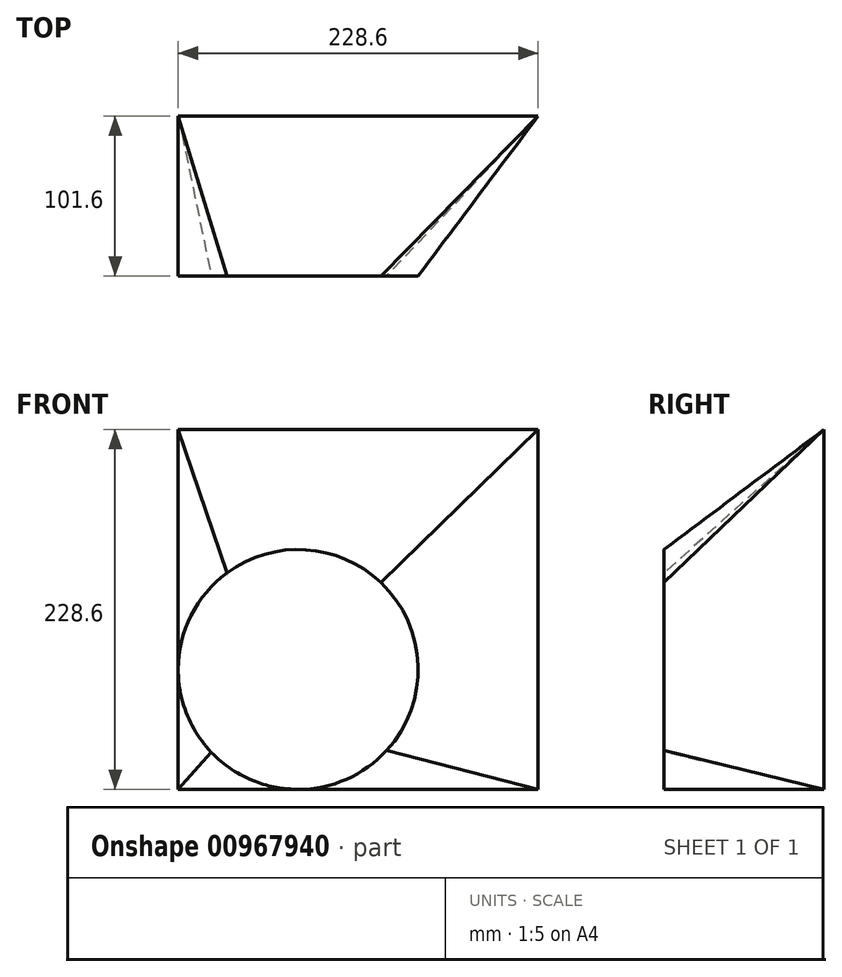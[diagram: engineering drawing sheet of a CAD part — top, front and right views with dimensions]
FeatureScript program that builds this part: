
annotation { "Feature Type Name" : "Feature", "Feature Type Description" : "" }
export const myFeature = defineFeature(function(context is Context, id is Id, definition is map)
    precondition{}
    {
        {
            var Q0;
            Q0=qCreatedBy(makeId("Front.planeOp"),FACE);
            var sketch = newSketch(context, id + "F0", { "sketchPlane" : qUnion([Q0])});
            skLineSegment(sketch, "E0.bottom", {"start": v(-114.3, 114.3) * mm, "end": v(114.3, 114.3) * mm});
            skLineSegment(sketch, "E0.top", {"start": v(-114.3, -114.3) * mm, "end": v(114.3, -114.3) * mm});
            skLineSegment(sketch, "E0.left", {"start": v(-114.3, 114.3) * mm, "end": v(-114.3, -114.3) * mm});
            skLineSegment(sketch, "E0.right", {"start": v(114.3, 114.3) * mm, "end": v(114.3, -114.3) * mm});
            skPoint(sketch, "E0.middle", {"position": v(0, 0) * mm});
            skSolve(sketch);
        }
        {
            var Q0;
            Q0=makeQuery(id+"F0.imprint","IMPRINT",FACE,{"disambiguationData":[TD([[makeQuery(id+"F0.imprint","IMPRINT",EDGE,{"derivedFrom":sQuery(id+"F0.wireOp",EDGE,"E0.bottom")}),-1.0]])]});
            cPlane(context, id + "F1", {"entities" : qUnion([Q0]), "cplaneType" : CPlaneType.OFFSET, "offset" : 101.6 * mm, "width" : 152.4 * mm, "height" : 152.4 * mm});
        }
        {
            var Q0;
            Q0=qCreatedBy(id+"F1.planeOp",FACE);
            var sketch = newSketch(context, id + "F2", { "sketchPlane" : qUnion([Q0])});
            skLineSegment(sketch, "E1", {"start": v(-114.3, 114.3) * mm, "end": v(-83.37, 23.2) * mm, "construction": true});
            skLineSegment(sketch, "E2", {"start": v(114.3, 114.3) * mm, "end": v(14.45, 17.08) * mm, "construction": true});
            skLineSegment(sketch, "E3", {"start": v(114.3, -114.3) * mm, "end": v(18.05, -89.62) * mm, "construction": true});
            skLineSegment(sketch, "E4", {"start": v(-114.3, -114.3) * mm, "end": v(-93.27, -90.66) * mm, "construction": true});
            skArc(sketch, "E5", {"start": v(-83.37, 23.2) * mm, "mid": v(-114.01, -31.5) * mm, "end": v(-93.27, -90.66) * mm});
            skArc(sketch, "E6", {"start": v(14.45, 17.08) * mm, "mid": v(-33.35, 37.95) * mm, "end": v(-83.37, 23.2) * mm});
            skLineSegment(sketch, "E7", {"start": v(18.05, -89.62) * mm, "end": v(18.05, -89.62) * mm});
            skLineSegment(sketch, "E8", {"start": v(14.45, 17.08) * mm, "end": v(14.45, 17.08) * mm});
            skArc(sketch, "E9", {"start": v(18.05, -89.62) * mm, "mid": v(38.06, -35.53) * mm, "end": v(14.45, 17.08) * mm});
            skArc(sketch, "E10", {"start": v(-93.27, -90.66) * mm, "mid": v(-37.39, -114.3) * mm, "end": v(18.05, -89.62) * mm});
            skLineSegment(sketch, "E11", {"start": v(-93.27, -90.66) * mm, "end": v(-93.27, -90.66) * mm});
            skLineSegment(sketch, "E12", {"start": v(-83.37, 23.2) * mm, "end": v(-83.37, 23.2) * mm});
            skSolve(sketch);
        }
        {
            var Q0;
            Q0=makeQuery(id+"F0.imprint","IMPRINT",FACE,{"disambiguationData":[TD([[makeQuery(id+"F0.imprint","IMPRINT",EDGE,{"derivedFrom":sQuery(id+"F0.wireOp",EDGE,"E0.bottom")}),-1.0]])]});
            var Q1;
            Q1=makeQuery(id+"F2.imprint","IMPRINT",FACE,{"disambiguationData":[TD([[makeQuery(id+"F2.imprint","IMPRINT",EDGE,{"derivedFrom":sQuery(id+"F2.wireOp",EDGE,"E5")}),1.0]])]});
            loft(context, id + "F3", {"sheetProfilesArray" : [{ "sheetProfileEntities" : qUnion([Q0]) }, { "sheetProfileEntities" : qUnion([Q1]) }]});
        }
    });
